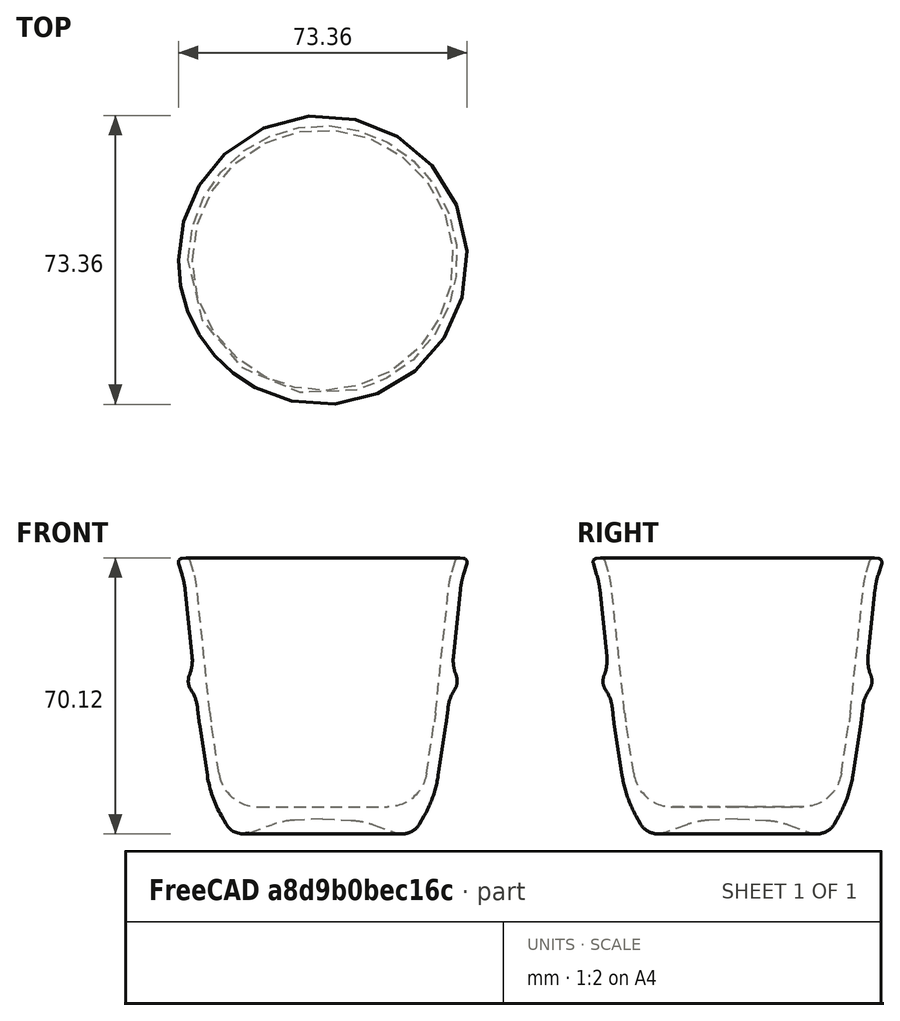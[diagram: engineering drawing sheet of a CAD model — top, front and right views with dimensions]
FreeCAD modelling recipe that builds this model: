
FCSTD DOCUMENT  (FreeCAD 0.21R)
Label: cup
License: All rights reserved
LicenseURL: http://en.wikipedia.org/wiki/All_rights_reserved
objects: Sketcher::SketchObject×1, PartDesign::Revolution×1, PartDesign::Body×1
note: 4 computed .brp shape members not serialized (recipe doc carries the construction recipe); baked Part::Feature solids carry a one-line shape summary decoded from their .brp

FEATURE [Sketcher::SketchObject] Sketch
  FullyConstrained = false
  MapMode = 5
  Placement = pos=(0,0,0) rot=(1,0,0;1.5708rad)
  Support = -> [XZ_Plane]
  sketch-geometry (26):
    g0: ArcOfCircle CenterX=-6.15398 CenterY=-16.5066 CenterZ=0 NormalX=0 NormalY=0 NormalZ=1 AngleXU=0 Radius=20 StartAngle=1.62316 EndAngle=1.91461
    g1: LineSegment StartX=-18.5661 StartY=0.292625 StartZ=0 EndX=-12.8956 EndY=2.32288 EndZ=0
    g2: ArcOfCircle CenterX=-20.2516 CenterY=5 CenterZ=0 NormalX=0 NormalY=0 NormalZ=1 AngleXU=0 Radius=5 StartAngle=3.6576 EndAngle=5.05621
    g3: ArcOfCircle CenterX=21.0609 CenterY=36.0157 CenterZ=0 NormalX=0 NormalY=0 NormalZ=1 AngleXU=0 Radius=50 StartAngle=3.24631 EndAngle=3.29362
    g4: ArcOfCircle CenterX=18.0847 CenterY=35.6315 CenterZ=0 NormalX=0 NormalY=0 NormalZ=1 AngleXU=0 Radius=50 StartAngle=3.24631 EndAngle=3.29362
    g5: ArcOfCircle CenterX=-54.8596 CenterY=59.9768 CenterZ=0 NormalX=0 NormalY=0 NormalZ=1 AngleXU=0 Radius=20 StartAngle=0.10472 EndAngle=0.302115
    g6: LineSegment StartX=-28.6652 StartY=30.7893 StartZ=0 EndX=-32.0167 EndY=62.6764 EndZ=0
    g7: ArcOfCircle CenterX=-51.9071 CenterY=60.5858 CenterZ=0 NormalX=0 NormalY=0 NormalZ=1 AngleXU=0 Radius=20 StartAngle=0.10472 EndAngle=0.302115
    g8: LineSegment StartX=-32.8129 StartY=66.5366 StartZ=0 EndX=-33.7102 EndY=69.4157 EndZ=0
    g9: ArcOfCircle CenterX=-34.6649 CenterY=69.1182 CenterZ=0 NormalX=0 NormalY=0 NormalZ=1 AngleXU=0 Radius=1 StartAngle=0.302115 EndAngle=1.67552
    g10: LineSegment StartX=-35.7837 StartY=70.0061 StartZ=0 EndX=-34.7695 EndY=70.1127 EndZ=0
    g11: LineSegment StartX=-35.7655 StartY=65.9276 StartZ=0 EndX=-36.6339 EndY=68.714 EndZ=0
    g12: ArcOfCircle CenterX=-35.6792 CenterY=69.0116 CenterZ=0 NormalX=0 NormalY=0 NormalZ=1 AngleXU=0 Radius=1 StartAngle=1.67552 EndAngle=3.44371
    g13: LineSegment StartX=-24.6005 StartY=2.53294 StartZ=0 EndX=-25.7497 EndY=4.55876 EndZ=0
    g14: LineSegment StartX=-29.3098 StartY=14.8178 StartZ=0 EndX=-31.3386 EndY=28.0593 EndZ=0
    g15: ArcOfCircle CenterX=0.344156 CenterY=19.3611 CenterZ=0 NormalX=0 NormalY=0 NormalZ=1 AngleXU=0 Radius=30 StartAngle=3.29362 EndAngle=3.6576
    g16: LineSegment StartX=0 StartY=6.84746 StartZ=0 EndX=0 EndY=3.84334 EndZ=0
    g17: LineSegment StartX=0 StartY=3.84334 StartZ=0 EndX=-7.2007 EndY=3.46597 EndZ=0
    g18: LineSegment StartX=-31.6414 StartY=30.4051 StartZ=0 EndX=-31.8107 EndY=32.0159 EndZ=0
    g19: ArcOfCircle CenterX=-41.7559 CenterY=30.9707 CenterZ=0 NormalX=0 NormalY=0 NormalZ=1 AngleXU=0 Radius=10 StartAngle=0.10472 EndAngle=0.595235
    g20: LineSegment StartX=-33.1894 StartY=45.134 StartZ=0 EndX=-34.9692 EndY=62.0673 EndZ=0
    g21: ArcOfCircle CenterX=-30.1637 CenterY=38.8205 CenterZ=0 NormalX=0 NormalY=0 NormalZ=1 AngleXU=0 Radius=4 StartAngle=2.7558 EndAngle=3.73683
    g22: ArcOfCircle CenterX=-43.1347 CenterY=44.0887 CenterZ=0 NormalX=0 NormalY=0 NormalZ=1 AngleXU=0 Radius=10 StartAngle=5.89739 EndAngle=6.38791
    g23: LineSegment StartX=0 StartY=6.84746 StartZ=0 EndX=-16.4691 EndY=6.84746 EndZ=0
    g24: LineSegment StartX=-26.3538 StartY=15.333 StartZ=0 EndX=-28.3624 EndY=28.4435 EndZ=0
    g25: ArcOfCircle CenterX=-16.4691 CenterY=16.8475 CenterZ=0 NormalX=0 NormalY=0 NormalZ=1 AngleXU=0 Radius=10 StartAngle=3.29362 EndAngle=4.71239
  constraints (26):
    c: Coincident(g11,g12)
    c: Coincident(g10,g12)
    c: Coincident(g5,g11)
    c: Coincident(g5,g20)
    c: Coincident(g9,g10)
    c: Coincident(g21,g22)
    c: Coincident(g8,g9)
    c: Coincident(g19,g21)
    c: Coincident(g20,g22)
    c: Coincident(g7,g8)
    c: Coincident(g6,g7)
    c: Coincident(g18,g19)
    c: Coincident(g4,g18)
    c: Coincident(g4,g14)
    c: Coincident(g14,g15)
    c: Coincident(g3,g6)
    c: Coincident(g3,g24)
    c: Coincident(g24,g25)
    c: Coincident(g13,g15)
    c: Coincident(g2,g13)
    c: Coincident(g1,g2)
    c: Coincident(g23,g25)
    c: Coincident(g0,g1)
    c: Coincident(g0,g17)
    c: Coincident(g16,g17)
    c: Coincident(g16,g23)
FEATURE [PartDesign::Revolution] Revolution
  Angle = 360
  Axis = (0,-2e-16,1)
  Base = (0,0,0)
  Placement = pos=(0,0,0) rot=(1,0,0;1.5708rad)
  Profile = -> Sketch
  ReferenceAxis = -> Sketch [V_Axis]
FEATURE [PartDesign::Body] Body  label="Corps"
  Group = -> [Sketch,Revolution]
  Origin = -> Origin
  Tip = -> Revolution
